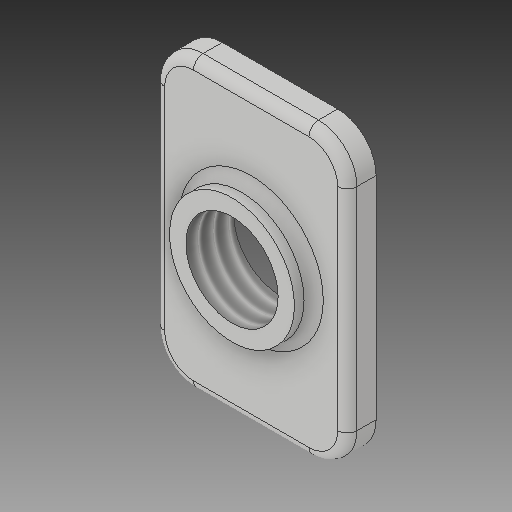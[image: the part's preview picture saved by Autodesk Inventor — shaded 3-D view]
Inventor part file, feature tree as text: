
AUTODESK INVENTOR PART (.ipt)
format: ipt  version: 2018 (Build 220112000, 112)  size: 177,152 bytes
history: native  units: mm
features: other x3, sketch x2
ambient origin geometry x8: Origin, YZ Plane, XZ Plane, XY Plane, X Axis, Y Axis, Z Axis, Center Point
bodies: Solid1 (feature_tree)
feature tree (5):
  other  "M5 Tee Nut-Generic_MIR_CPY.ipt"
  other  "Solid1::M5 Tee Nut-Generic_MIR_CPY.ipt"
  other  "TaggingFeature1"
  sketch  "Sketch1"  dims[d0=10.0mm]
  sketch  "Sketch2"
